# Revit family: R-BGF-060
name_source: partatom
category: Portes
units: mm (PartAtom-declared; Revit-internal decimal feet)

## family parameters
Couper avec des vides une fois chargée = Non
Hôte = Mur
Partagée = Non
Point de calcul de pièce = Oui
Toujours verticalement = Oui

## types (1)
- R-BGF-060
    ----- EQUIPEMENTS ----------------------- = .
    ----- PARAMETRES DE L'HÔTE -------------------- = .
    ----- PARAMETRES DES VANTAUX -------------------- = .
    ----- PARAMETRES POSITION HUISSERIE -------------------- = .
    ----- PARAMETRES PROFIL HUISSERIE -------------------- = .
    ----- TYPE DE VANTAIL -------------------- = .
    ----PARAMETRES INUTILISES------------------------- = .
    1 Vantail = Oui
    2 Vantaux = Non
    Coloris Oculus = Lauan - Meranti
    Coloris Oculus Métal = Acier - finition peinture thermolaque - gris - brillant
    Coloris_Chants = BER
    Construction analytique = <Aucun>
    DAS = Non
    Description = Bloc-gaine 1 vantail sous imposte, en MDF, EI30, sur huisserie bois
    Décalage Largeur Paumelle Recouvrement = 0 mm  [stored 0 ft]
    Décalage_Seuil_Vantail = 0 mm  [stored 0 ft]
    Désaffleurement_Vantail = 0 mm  [stored 0 ft]
    Epaisseurs_Vantaux = 40 mm  [stored 0.131234 ft]
    Espacement_Paumelle_Vantail = 5 mm  [stored 0.0164042 ft]
    Fabricant = Montibert
    Ferrage encastré = Oui
    Ferrage_Encastre = Non
    Fiche_Produit = BGF-060
    Hauteur Feuillure Basse Vantail = 15 mm  [stored 0.0492126 ft]
    Hauteur_Axe_Bequille = 1000 mm  [stored 3.28084 ft]
    Hauteur_Vantaux_Souhaitée = 2000 mm  [stored 6.56168 ft]
    Inv_Espacement_Paumelle_Vantail = 10 mm  [stored 0.0328084 ft]
    Inv_Position_Largeur_Paumelle = 5 mm  [stored 0.0164042 ft]
    Jeu Profondeur Recouvrement Vantail = 0 mm  [stored 0 ft]
    Jeu_Côté_Articulation_Vantail = 2 mm  [stored 0.00656168 ft]
    Jeu_Côté_Fermeture_Vantail = 2 mm  [stored 0.00656168 ft]
    Jeu_Traverse_Basse_Vantail = 3 mm  [stored 0.00984252 ft]
    Jeu_Traverse_Haute_Vantail = 3 mm  [stored 0.00984252 ft]
    Largeur Feuillure Battement Articulation = 15 mm  [stored 0.0492126 ft]
    Largeur_Axe_Bequille = 50 mm  [stored 0.164042 ft]
    Largeur_Feuillure_Battement_Semi_Fixe = 15 mm  [stored 0.0492126 ft]
    Largeur_Feuillure_Battement_Service = 15 mm  [stored 0.0492126 ft]
    Largeur_Feuillure_Profil = 20 mm  [stored 0.0656168 ft]
    Largeur_Vantail_Semi_Fixe_Souhaitée = 530 mm  [stored 1.73885 ft]
    Largeur_Vantail_Service_Souhaitée = 630 mm  [stored 2.06693 ft]
    Materiaux_Dominant = Bois
    Modèle = 04-Gaine
    NON = Non
    Note d'identification = 1 VANTAIL SOUS IMPOSTE
    OUI = Oui
    Paumelle = Oui
    Paumelle_1 = 230 mm  [stored 0.754593 ft]
    Paumelle_2 = 809 mm  [stored 2.6542 ft]
    Paumelle_3 = 809 mm  [stored 2.6542 ft]
    Paumelle_4 = 0 mm  [stored 0 ft]
    Position_Largeur_Paumelle = 0 mm  [stored 0 ft]
    Profil Battement_Ep Joint = 3 mm  [stored 0.00984252 ft]
    Profil Battement_Hauteur = 1960 mm  [stored 6.43045 ft]
    Profil Battement_Largeur = 80 mm  [stored 0.262467 ft]
    Profil Battement_Largeur Feuillure Coté 1 = 15 mm  [stored 0.0492126 ft]
    Profil Battement_Largeur Feuillure Coté 2 = 15 mm  [stored 0.0492126 ft]
    Profil Battement_Profondeur = 78 mm  [stored 0.255906 ft]
    Profil Battement_Profondeur Décalage Vantail Coté Paumelle = 15 mm  [stored 0.0492126 ft]
    Profil Battement_Profondeur Feuillure Coté 1 = 25 mm  [stored 0.082021 ft]
    Profil Battement_Profondeur Feuillure Coté 2 = 25 mm  [stored 0.082021 ft]
    Profil de Battement = Non
    Profondeur Feuillure Basse Vantail = 25 mm  [stored 0.082021 ft]
    Profondeur Feuillure Battement Articulation = 25 mm  [stored 0.082021 ft]
    Profondeur_Feuillure_Battement_Semi_Fixe = 15 mm  [stored 0.0492126 ft]
    Profondeur_Feuillure_Battement_Service = 25 mm  [stored 0.082021 ft]
    Profondeur_Feuillure_Profil = 40 mm  [stored 0.131234 ft]
    Reference_Commerciale = BG 1V EI30
    Reprise_Doublage_1 = 30 mm  [stored 0.0984252 ft]
    Reprise_Doublage_2 = 30 mm  [stored 0.0984252 ft]
    Reprise_Doublage_Haut = 30 mm  [stored 0.0984252 ft]
    Resistance_Feu = E30-EI30
    Sens_Feu = Recto / Verso
    Serrure 3 points = Oui
    Thermique (W/m2.°K) = 0
    URL = https://www.malerba.fr
    Vantail à Recouvrement = Non
    Visibilite_Serrure = Oui
    X_Décalage Hauteur Feuillure Recouvrement = 0 mm  [stored 0 ft]
    X_Décalage Largeur Feuillure Recouvrement = 0 mm  [stored 0 ft]
    X_Décalage Largeur Recouvrement Vantail = 0 mm  [stored 0 ft]
    X_Décalage Profondeur Recouvrement Vantail = 0 mm  [stored 0 ft]
    X_Espacement_Paumelle_Vantail = 5 mm  [stored 0.0164042 ft]
    X_Inv Décalage Profondeur Recouvrement Vantail = 0 mm  [stored 0 ft]
    X_Inv_Espacement_Paumelle_Vantail = 0 mm  [stored 0 ft]
    X_Inv_Position_Largeur_Paumelle = 0 mm  [stored 0 ft]
    X_Paumelle = Oui
    X_Vantail_Hauteur_Recouvrement sur Huisserie = 0 mm  [stored 0 ft]
    X_Visibilite_Paum-4 = Non

note: [stored X ft] marks values corroborated as IEEE doubles in the binary element streams (Revit-internal decimal feet)

## geometry (parser evidence)
native form markers: Blend x14
no freeform markers — native parametric forms only
